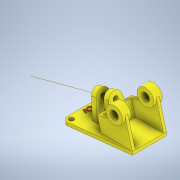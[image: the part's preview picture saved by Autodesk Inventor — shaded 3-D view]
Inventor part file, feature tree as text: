
AUTODESK INVENTOR PART (.ipt)
format: ipt  version: 2021 (Build 250183000, 183)  size: 332,288 bytes
history: native  units: mm
features: sketch x12, extrude x7, hole x4, other x2, emboss x1
ambient origin geometry x8: Origin, YZ Plane, XZ Plane, XY Plane, X Axis, Y Axis, Z Axis, Center Point
bodies: Solid1 (feature_tree)
feature tree (26):
  other  "Work Axis1"
  extrude  "Extrusion1"  Depth=14.0mm
  extrude  "Extrusion2"  Depth=12.0mm
  extrude  "Extrusion3"  Depth=117.0mm
  extrude  "Extrusion4"  Depth=13.613568mm
  extrude  "Extrusion5"  Depth=15.0mm
  extrude  "Extrusion6"  Depth=49.0mm
  extrude  "Extrusion7"  Depth=25.3mm
  hole  "Hole4"  [1 undecoded]
  hole  "Hole5"  [1 undecoded]
  hole  "Hole6"  [1 undecoded]
  hole  "Hole7"  [1 undecoded]
  emboss  "Emboss1"
  other  "Work Point1"
  sketch  "Sketch1"  dims[d6=9.0mm d7=14.0mm]
  sketch  "Sketch2"  dims[d8=9.0mm d9=12.0mm]
  sketch  "Sketch4"  dims[d10=35.0mm d11=117.0mm]
  sketch  "Sketch5"  dims[d12=50.0mm d13=0.0mm d14=13.613568mm]
  sketch  "Sketch6"  dims[d15=13.613568mm d16=15.0mm]
  sketch  "Sketch7"  dims[d17=50.0mm d18=0.0mm d19=49.0mm]
  sketch  "Sketch8"  dims[d20=30.0mm d21=25.3mm]
  sketch  "Sketch12"  dims[d22=5.0mm d23=61.0mm d24=0.0mm]
  sketch  "Sketch13"  dims[d25=5.0mm d26=5.0mm]
  sketch  "Sketch14"  dims[d27=5.0mm d28=5.0mm]
  sketch  "Sketch15"  dims[d29=0.0mm d30=0.0mm d34=71.0mm d35=0.0mm]
  sketch  "Sketch16"  dims[d36=39.0mm d37=41.0mm d38=0.0mm d39=8.0mm d40=113.0mm d41=70.0mm d42=35.0mm d43=6.0mm d44=0.0mm d66=15.0mm d67=6.0mm d68=4.0mm d69=2.0mm d70=90.0deg d71=8.0mm d72=20.594885mm d73=9.0mm d74=6.0mm d75=4.0mm d76=2.0mm d77=90.0deg d78=8.0mm d79=20.594885mm d80=9.0mm d81=6.0mm d82=4.0mm d83=2.0mm d84=90.0deg d85=8.0mm d86=20.594885mm d87=9.0mm d88=6.0mm d89=4.0mm d90=2.0mm d91=90.0deg d92=8.0mm d93=20.594885mm d94=15.0mm d95=29.0mm d96=11.0mm d97=1.0mm d98=0.0mm d45=0.25mm d46=0.375mm d47=14.3117mm d48=0.75mm d49=20.594885mm d50=0.0625mm d51=0.75mm d52=0.375mm d53=1.0mm d54=1.0mm d55=0.15mm d56=0.25mm d57=0.375mm d58=14.3117mm d59=0.75mm d60=20.594885mm d61=0.0625mm d62=0.75mm d63=0.375mm]
note: 4 required parameter values undecoded (feature->parameter linkage not recoverable at this tier; creation-order binding heuristic only, values carry confidence <= 0.55)
